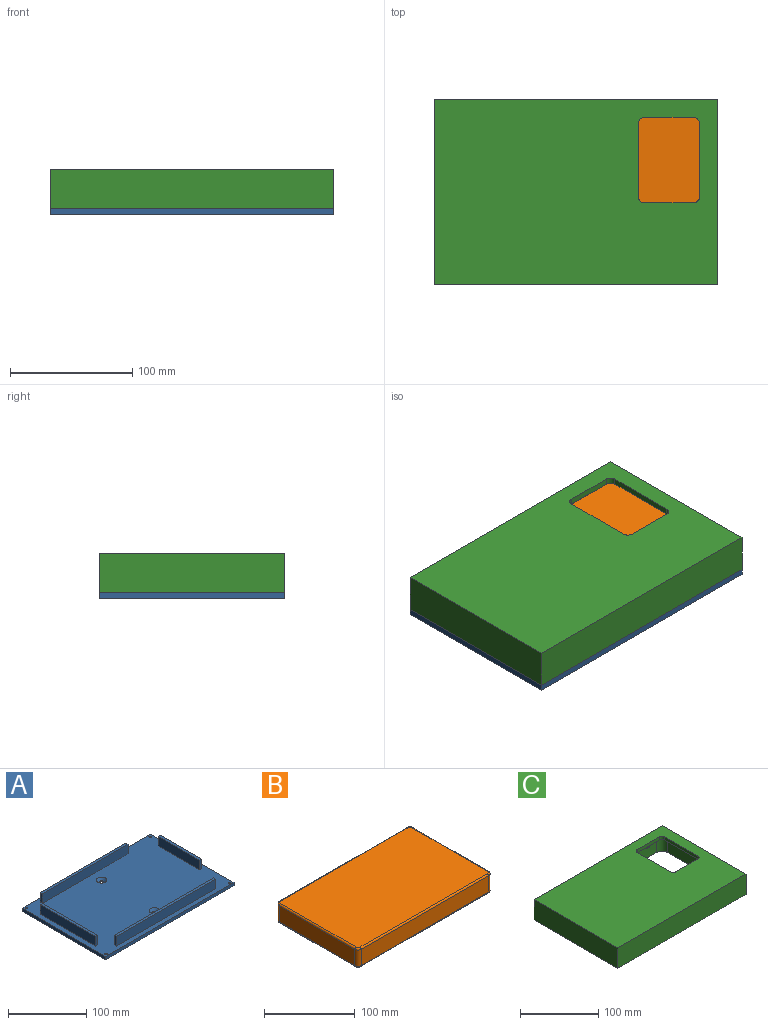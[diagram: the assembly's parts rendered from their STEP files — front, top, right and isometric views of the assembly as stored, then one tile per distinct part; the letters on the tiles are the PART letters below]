
ASSEMBLY  parts=3 mates=2
PART A: 42 faces, bbox 232x152x20 mm
  f0: plane 232x152mm, normal (0,0,1), area 32913.8mm2, adj f1,f2,f3,f4,f6,f7,f8,f9
  f1: plane 232x5mm, normal (0,1,0), area 1160mm2, adj f0,f2,f4,f5
  f2: plane 152x5mm, normal (-1,0,0), area 760mm2, adj f0,f1,f3,f5
  f3: plane 232x5mm, normal (0,-1,0), area 1160mm2, adj f0,f2,f4,f5
  f4: plane 152x5mm, normal (1,0,0), area 760mm2, adj f0,f1,f3,f5
  f5: plane 232x152mm, normal (0,0,-1), area 35100.5mm2, adj f1,f2,f3,f4,f28,f31,f34,f37
  f6: plane 15x4mm, normal (-1,0,0), area 60mm2, adj f0,f7,f9,f10
  f7: plane 155x15mm, normal (0,-1,0), area 2325mm2, adj f0,f6,f8,f10
  f8: plane 15x4mm, normal (1,0,0), area 60mm2, adj f0,f7,f9,f10
  f9: plane 155x15mm, normal (0,1,0), area 2325mm2, adj f0,f6,f8,f10
  f10: plane 155x4mm, normal (0,0,1), area 620mm2, adj f6,f7,f8,f9
  f11: plane 180x15mm, normal (0,1,0), area 2700mm2, adj f0,f12,f14,f15
  f12: plane 15x4mm, normal (-1,0,0), area 60mm2, adj f0,f11,f13,f15
  f13: plane 180x15mm, normal (0,-1,0), area 2700mm2, adj f0,f12,f14,f15
  f14: plane 15x4mm, normal (1,0,0), area 60mm2, adj f0,f11,f13,f15
  f15: plane 180x4mm, normal (0,0,1), area 720mm2, adj f11,f12,f13,f14
  f16: plane 100x15mm, normal (1,0,0), area 1500mm2, adj f0,f17,f19,f20
  f17: plane 15x4mm, normal (0,1,0), area 60mm2, adj f0,f16,f18,f20
  f18: plane 100x15mm, normal (-1,0,0), area 1500mm2, adj f0,f17,f19,f20
  f19: plane 15x4mm, normal (0,-1,0), area 60mm2, adj f0,f16,f18,f20
  f20: plane 100x4mm, normal (0,0,1), area 400mm2, adj f16,f17,f18,f19
  f21: plane 15x4mm, normal (0,1,0), area 60mm2, adj f0,f22,f24,f25
  f22: plane 75x15mm, normal (-1,0,0), area 1125mm2, adj f0,f21,f23,f25
  f23: plane 15x4mm, normal (0,-1,0), area 60mm2, adj f0,f22,f24,f25
  f24: plane 75x15mm, normal (1,0,0), area 1125mm2, adj f0,f21,f23,f25
  f25: plane 75x4mm, normal (0,0,1), area 300mm2, adj f21,f22,f23,f24
  f26: cylinder r=1.45mm len=2.9mm, axis (0,0,-1), area 22.8mm2, adj f0,f27
  f27: plane 5.5x5.5mm, normal (0,0,-1), area 17.2mm2, adj f26,f28
  f28: cylinder r=2.75mm len=5.5mm, axis (0,0,-1), area 43.2mm2, adj f5,f27
  f29: cylinder r=1.45mm len=2.9mm, axis (0,0,-1), area 22.8mm2, adj f0,f30
  f30: plane 5.5x5.5mm, normal (0,0,-1), area 17.2mm2, adj f29,f31
  f31: cylinder r=2.75mm len=5.5mm, axis (0,0,-1), area 43.2mm2, adj f5,f30
  f32: cylinder r=1.45mm len=2.9mm, axis (0,0,-1), area 22.8mm2, adj f0,f33
  f33: plane 5.5x5.5mm, normal (0,0,-1), area 17.2mm2, adj f32,f34
  f34: cylinder r=2.75mm len=5.5mm, axis (0,0,-1), area 43.2mm2, adj f5,f33
  f35: cylinder r=1.45mm len=2.9mm, axis (0,0,-1), area 22.8mm2, adj f0,f36
  f36: plane 5.5x5.5mm, normal (0,0,-1), area 17.2mm2, adj f35,f37
  f37: cylinder r=2.75mm len=5.5mm, axis (0,0,-1), area 43.2mm2, adj f5,f36
  f38: cylinder r=3.3mm len=6.6mm, axis (0,0,1), area 32.8mm2, adj f5,f39
  f39: cone r=3.3mm half-angle=45deg, axis (0,0,1), area 152.3mm2, adj f0,f38
  f40: cylinder r=3.3mm len=6.6mm, axis (0,0,1), area 32.8mm2, adj f5,f41
  f41: cone r=3.3mm half-angle=45deg, axis (0,0,1), area 152.3mm2, adj f0,f40
PART B: 26 faces, bbox 209.8x128.8x26 mm
  f0: plane 199x22mm, normal (0,1,0), area 4378mm2, adj f6,f9,f17,f25
  f1: plane 118x22mm, normal (-1,0,0), area 2596mm2, adj f6,f7,f13,f21
  f2: plane 199x22mm, normal (0,-1,0), area 4378mm2, adj f7,f8,f10,f18
  f3: plane 118x22mm, normal (1,0,0), area 2596mm2, adj f8,f9,f14,f22
  f4: plane 205x124mm, normal (0,0,1), area 25412.3mm2, adj f10,f11,f12,f13,f14,f15,f16,f17
  f5: plane 205x124mm, normal (0,0,-1), area 25412.3mm2, adj f18,f19,f20,f21,f22,f23,f24,f25
  f6: cylinder r=5mm len=22mm, axis (0,0,1), area 172.8mm2, adj f0,f1,f15,f23
  f7: cylinder r=5mm len=22mm, axis (0,0,-1), area 172.8mm2, adj f1,f2,f11,f19
  f8: cylinder r=5mm len=22mm, axis (0,0,1), area 172.8mm2, adj f2,f3,f12,f20
  f9: cylinder r=5mm len=22mm, axis (0,0,-1), area 172.8mm2, adj f0,f3,f16,f24
  f10: cylinder r=2mm len=199mm, axis (-1,0,0), area 625.2mm2, adj f2,f4,f11,f12
  f11: torus R=3mm, axis (0,0,1), area 21.1mm2, adj f4,f7,f10,f13
  f12: torus R=3mm, axis (0,0,1), area 21.1mm2, adj f4,f8,f10,f14
  f13: cylinder r=2mm len=118mm, axis (0,1,0), area 370.7mm2, adj f1,f4,f11,f15
  f14: cylinder r=2mm len=118mm, axis (0,-1,0), area 370.7mm2, adj f3,f4,f12,f16
  f15: torus R=3mm, axis (0,0,1), area 21.1mm2, adj f4,f6,f13,f17
  f16: torus R=3mm, axis (0,0,1), area 21.1mm2, adj f4,f9,f14,f17
  f17: cylinder r=2mm len=199mm, axis (1,0,0), area 625.2mm2, adj f0,f4,f15,f16
  f18: cylinder r=2mm len=199mm, axis (1,0,0), area 625.2mm2, adj f2,f5,f19,f20
  f19: torus R=3mm, axis (0,0,1), area 21.1mm2, adj f5,f7,f18,f21
  f20: torus R=3mm, axis (0,0,1), area 21.1mm2, adj f5,f8,f18,f22
  f21: cylinder r=2mm len=118mm, axis (0,-1,0), area 370.7mm2, adj f1,f5,f19,f23
  f22: cylinder r=2mm len=118mm, axis (0,1,0), area 370.7mm2, adj f3,f5,f20,f24
  f23: torus R=3mm, axis (0,0,1), area 21.1mm2, adj f5,f6,f21,f25
  f24: torus R=3mm, axis (0,0,1), area 21.1mm2, adj f5,f9,f22,f25
  f25: cylinder r=2mm len=199mm, axis (-1,0,0), area 625.2mm2, adj f0,f5,f23,f24
PART C: 33 faces, bbox 232x152x32 mm
  f0: plane 232x152mm, normal (0,0,1), area 31785.5mm2, adj f3,f4,f5,f6,f15,f16,f17,f18
  f1: plane 222x142mm, normal (0,0,-1), area 27959.6mm2, adj f7,f8,f9,f10,f11,f12,f13,f14
  f2: plane 232x152mm, normal (0,0,-1), area 3811.3mm2, adj f3,f4,f5,f6,f7,f8,f9,f10
  f3: plane 232x32mm, normal (0,1,0), area 7341.2mm2, adj f0,f2,f4,f6,f32
  f4: plane 152x32mm, normal (-1,0,0), area 4864mm2, adj f0,f2,f3,f5
  f5: plane 232x32mm, normal (0,-1,0), area 7424mm2, adj f0,f2,f4,f6
  f6: plane 152x32mm, normal (1,0,0), area 4785.5mm2, adj f0,f2,f3,f5,f31
  f7: plane 202x27mm, normal (0,1,0), area 5454mm2, adj f1,f2,f11,f14
  f8: plane 122x27mm, normal (1,0,0), area 3294mm2, adj f1,f2,f11,f12
  f9: plane 202x27mm, normal (0,-1,0), area 5371.2mm2, adj f1,f2,f12,f13,f32
  f10: plane 122x27mm, normal (-1,0,0), area 3215.5mm2, adj f1,f2,f13,f14,f31
  f11: cylinder r=10mm len=27mm, axis (0,0,-1), area 424.1mm2, adj f1,f2,f7,f8
  f12: cylinder r=10mm len=27mm, axis (0,0,1), area 424.1mm2, adj f1,f2,f8,f9
  f13: cylinder r=10mm len=27mm, axis (0,0,-1), area 424.1mm2, adj f1,f2,f9,f10
  f14: cylinder r=10mm len=27mm, axis (0,0,1), area 424.1mm2, adj f1,f2,f7,f10
  f15: plane 60x5mm, normal (-1,0,0), area 300mm2, adj f0,f1,f27,f30
  f16: plane 40x5mm, normal (0,-1,0), area 200mm2, adj f0,f1,f27,f28
  f17: plane 60x5mm, normal (1,0,0), area 300mm2, adj f0,f1,f28,f29
  f18: plane 40x5mm, normal (0,1,0), area 200mm2, adj f0,f1,f29,f30
  f19: cone r=0mm half-angle=59deg, axis (0,0,-1), area 4.2mm2, adj f20
  f20: cylinder r=1.07mm len=10.67mm, axis (0,0,-1), area 72.1mm2, adj f2,f19
  f21: cone r=0mm half-angle=59deg, axis (0,0,-1), area 4.2mm2, adj f22
  f22: cylinder r=1.07mm len=10.67mm, axis (0,0,-1), area 72.1mm2, adj f2,f21
  f23: cone r=0mm half-angle=59deg, axis (0,0,-1), area 4.2mm2, adj f24
  f24: cylinder r=1.07mm len=10.67mm, axis (0,0,-1), area 72.1mm2, adj f2,f23
  f25: cone r=0mm half-angle=59deg, axis (0,0,-1), area 4.2mm2, adj f26
  f26: cylinder r=1.07mm len=10.67mm, axis (0,0,-1), area 72.1mm2, adj f2,f25
  f27: cylinder r=5mm len=5mm, axis (0,0,1), area 39.3mm2, adj f0,f1,f15,f16
  f28: cylinder r=5mm len=5mm, axis (0,0,-1), area 39.3mm2, adj f0,f1,f16,f17
  f29: cylinder r=5mm len=5mm, axis (0,0,1), area 39.3mm2, adj f0,f1,f17,f18
  f30: cylinder r=5mm len=5mm, axis (0,0,-1), area 39.3mm2, adj f0,f1,f15,f18
  f31: cylinder r=5mm len=10mm, axis (1,0,0), area 157.1mm2, adj f6,f10
  f32: cylinder r=5.13mm len=10.27mm, axis (0,1,0), area 161.3mm2, adj f3,f9
PLACE A t=(0.09,0.66,46)mm
PLACE B t=(0.09,0.66,51)mm
PLACE C t=(0.09,0.66,51)mm
MATE parallel A.f0 <-> B.f5  axis (0,0,1) through (0.65,0.75,51)mm
MATE cylindrical C.f21 <-> A.f35  axis (0,0,-1) through (-111.91,72.66,51)mm
